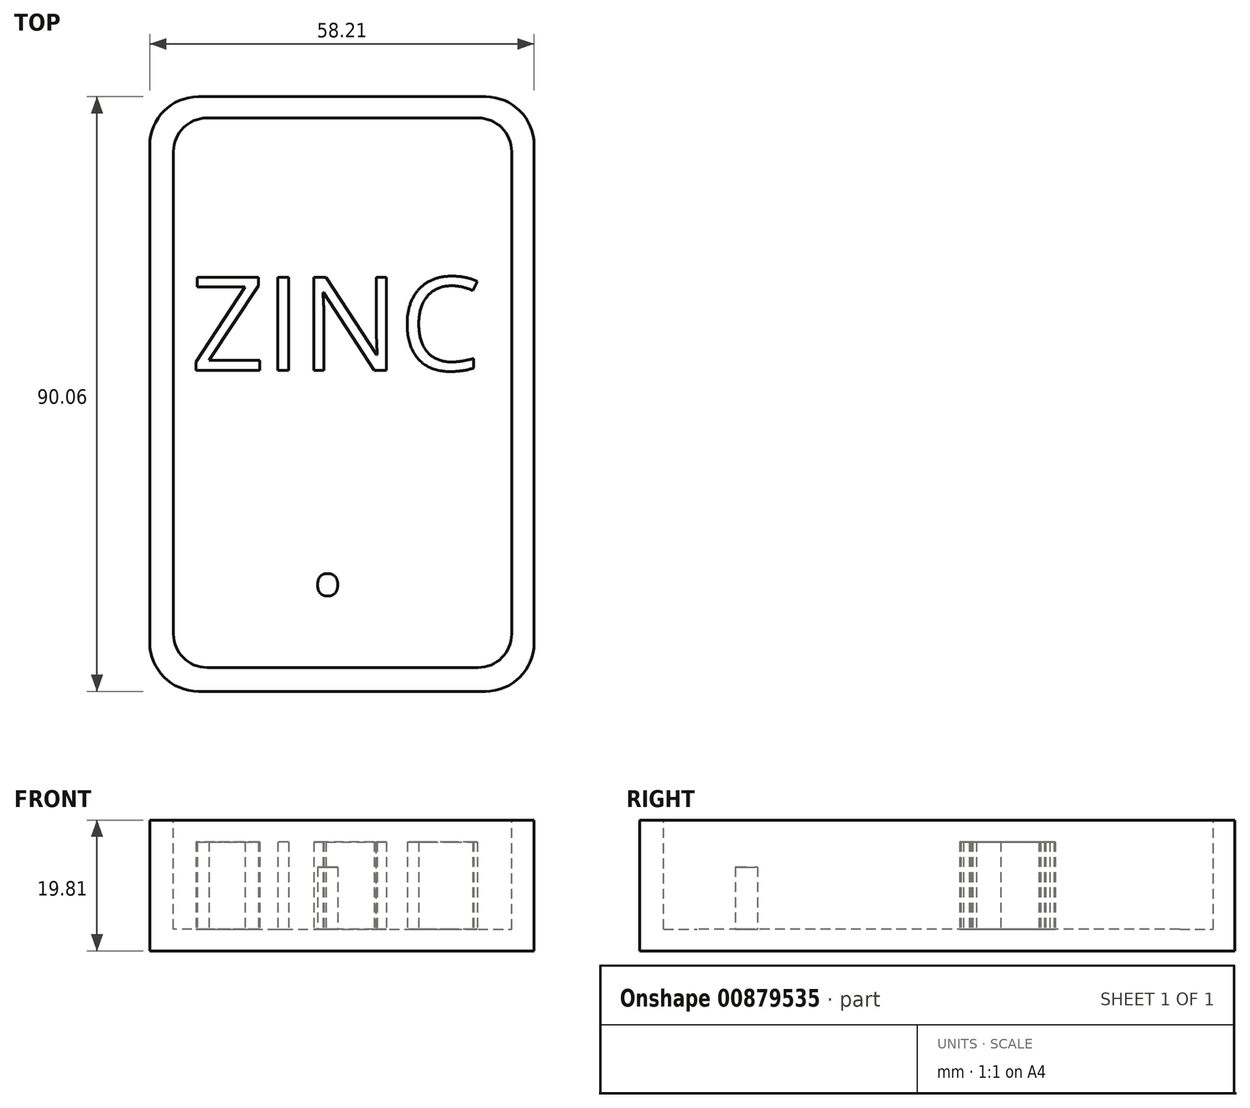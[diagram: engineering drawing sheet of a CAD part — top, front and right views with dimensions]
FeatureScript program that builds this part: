
annotation { "Feature Type Name" : "Feature", "Feature Type Description" : "" }
export const myFeature = defineFeature(function(context is Context, id is Id, definition is map)
    precondition{}
    {
        {
            var Q0;
            Q0=qCreatedBy(makeId("Top.planeOp"),FACE);
            var sketch = newSketch(context, id + "F0", { "sketchPlane" : qUnion([Q0])});
            skLineSegment(sketch, "E0.bottom", {"start": v(-21.7, 41.43) * mm, "end": v(36.5, 41.43) * mm});
            skLineSegment(sketch, "E0.top", {"start": v(-21.7, -48.63) * mm, "end": v(36.5, -48.63) * mm});
            skLineSegment(sketch, "E0.left", {"start": v(-21.7, 41.43) * mm, "end": v(-21.7, -48.63) * mm});
            skLineSegment(sketch, "E0.right", {"start": v(36.5, 41.43) * mm, "end": v(36.5, -48.63) * mm});
            skSolve(sketch);
        }
        {
            var Q0;
            Q0 = qSketchRegion(id + "F0", true);
            extrude(context, id + "F1", {"entities" : qUnion([Q0]), "depth" : 19.8 * mm, "offsetDistance" : 25.4 * mm});
        }
        {
            var Q0;
            Q0=makeQuery(id+"F1.opExtrude","CAP_FACE",FACE,{"disambiguationData":[OSD([sQuery(id+"F0.wireOp",EDGE,"E0.bottom"),sQuery(id+"F0.wireOp",EDGE,"E0.top"),sQuery(id+"F0.wireOp",EDGE,"E0.left"),sQuery(id+"F0.wireOp",EDGE,"E0.right")])],"isStart":false});
            var sketch = newSketch(context, id + "F2", { "sketchPlane" : qUnion([Q0])});
            skLineSegment(sketch, "E1.bottom", {"start": v(-18.1, 38.2) * mm, "end": v(33.08, 38.2) * mm});
            skLineSegment(sketch, "E1.top", {"start": v(-18.1, -45.03) * mm, "end": v(33.08, -45.03) * mm});
            skLineSegment(sketch, "E1.left", {"start": v(-18.1, 38.2) * mm, "end": v(-18.1, -45.03) * mm});
            skLineSegment(sketch, "E1.right", {"start": v(33.08, 38.2) * mm, "end": v(33.08, -45.03) * mm});
            skSolve(sketch);
        }
        {
            var Q0;
            Q0 = qSketchRegion(id + "F2", true);
            extrude(context, id + "F3", {"entities" : qUnion([Q0]), "operationType" : NewBodyOperationType.REMOVE, "oppositeDirection" : true, "depth" : 16.5 * mm, "offsetDistance" : 25.4 * mm});
        }
        {
            var Q0;
            Q0=makeQuery(id+"F1.opExtrude","SWEPT_EDGE",EDGE,{"disambiguationData":[OSD([sQuery(id+"F0.wireOp",EDGE,"E0.top"),sQuery(id+"F0.wireOp",EDGE,"E0.right")])]});
            var Q1;
            Q1=makeQuery(id+"F1.opExtrude","SWEPT_EDGE",EDGE,{"disambiguationData":[OSD([sQuery(id+"F0.wireOp",EDGE,"E0.top"),sQuery(id+"F0.wireOp",EDGE,"E0.left")])]});
            var Q2;
            Q2=makeQuery(id+"F1.opExtrude","SWEPT_EDGE",EDGE,{"disambiguationData":[OSD([sQuery(id+"F0.wireOp",EDGE,"E0.bottom"),sQuery(id+"F0.wireOp",EDGE,"E0.left")])]});
            var Q3;
            Q3=makeQuery(id+"F1.opExtrude","SWEPT_EDGE",EDGE,{"disambiguationData":[OSD([sQuery(id+"F0.wireOp",EDGE,"E0.bottom"),sQuery(id+"F0.wireOp",EDGE,"E0.right")])]});
            fillet(context, id + "F4", {"entities" : qUnion([Q0, Q1, Q2, Q3]), "radius" : 7.36 * mm, "tangentPropagation" : true, "allowEdgeOverflow" : false});
        }
        {
            var Q0;
            Q0=makeQuery(id+"F3.boolean.opBoolean","COPY",EDGE,{"derivedFrom":makeQuery(id+"F3.opExtrude","SWEPT_EDGE",EDGE,{"disambiguationData":[OSD([sQuery(id+"F2.wireOp",EDGE,"E1.bottom"),sQuery(id+"F2.wireOp",EDGE,"E1.right")])]})});
            var Q1;
            Q1=makeQuery(id+"F3.boolean.opBoolean","COPY",EDGE,{"derivedFrom":makeQuery(id+"F3.opExtrude","SWEPT_EDGE",EDGE,{"disambiguationData":[OSD([sQuery(id+"F2.wireOp",EDGE,"E1.bottom"),sQuery(id+"F2.wireOp",EDGE,"E1.left")])]})});
            var Q2;
            Q2=makeQuery(id+"F3.boolean.opBoolean","COPY",EDGE,{"derivedFrom":makeQuery(id+"F3.opExtrude","SWEPT_EDGE",EDGE,{"disambiguationData":[OSD([sQuery(id+"F2.wireOp",EDGE,"E1.top"),sQuery(id+"F2.wireOp",EDGE,"E1.left")])]})});
            var Q3;
            Q3=makeQuery(id+"F3.boolean.opBoolean","COPY",EDGE,{"derivedFrom":makeQuery(id+"F3.opExtrude","SWEPT_EDGE",EDGE,{"disambiguationData":[OSD([sQuery(id+"F2.wireOp",EDGE,"E1.top"),sQuery(id+"F2.wireOp",EDGE,"E1.right")])]})});
            fillet(context, id + "F5", {"entities" : qUnion([Q0, Q1, Q2, Q3]), "radius" : 5.08 * mm, "tangentPropagation" : true, "allowEdgeOverflow" : false});
        }
        {
            var Q0;
            Q0=makeQuery(id+"F3.boolean.opBoolean","COPY",FACE,{"derivedFrom":makeQuery(id+"F3.opExtrude","CAP_FACE",FACE,{"disambiguationData":[OSD([sQuery(id+"F2.wireOp",EDGE,"E1.bottom"),sQuery(id+"F2.wireOp",EDGE,"E1.top"),sQuery(id+"F2.wireOp",EDGE,"E1.left"),sQuery(id+"F2.wireOp",EDGE,"E1.right")])],"isStart":false})});
            var sketch = newSketch(context, id + "F6", { "sketchPlane" : qUnion([Q0])});
            skText(sketch, "E2", { "text": "ZINC\n", "fontName": "OpenSans-Regular.ttf"});
            const initialGuessF6  = {"E2": [-0.01551, 0, 1, 0, 0.01418]};
            skSetInitialGuess(sketch, initialGuessF6);
            skSolve(sketch);
        }
        {
            var Q0;
            Q0 = qSketchRegion(id + "F6", true);
            extrude(context, id + "F7", {"entities" : qUnion([Q0]), "operationType" : NewBodyOperationType.ADD, "depth" : 13.2 * mm, "offsetDistance" : 25.4 * mm});
        }
        {
            var Q0;
            Q0=makeQuery(id+"F3.boolean.opBoolean","COPY",FACE,{"derivedFrom":makeQuery(id+"F3.opExtrude","CAP_FACE",FACE,{"disambiguationData":[OSD([sQuery(id+"F2.wireOp",EDGE,"E1.bottom"),sQuery(id+"F2.wireOp",EDGE,"E1.top"),sQuery(id+"F2.wireOp",EDGE,"E1.left"),sQuery(id+"F2.wireOp",EDGE,"E1.right")])],"isStart":false})});
            var sketch = newSketch(context, id + "F8", { "sketchPlane" : qUnion([Q0])});
            skText(sketch, "E3", { "text": ".", "fontName": "OpenSans-Regular.ttf"});
            const initialGuessF8  = {"E3": [0.0018, -0.03384, 1, 0, 0.01858]};
            skSetInitialGuess(sketch, initialGuessF8);
            skSolve(sketch);
        }
        {
            var Q0;
            Q0 = qSketchRegion(id + "F8", true);
            extrude(context, id + "F9", {"entities" : qUnion([Q0]), "operationType" : NewBodyOperationType.ADD, "depth" : 9.4 * mm, "offsetDistance" : 25.4 * mm});
        }
    });
